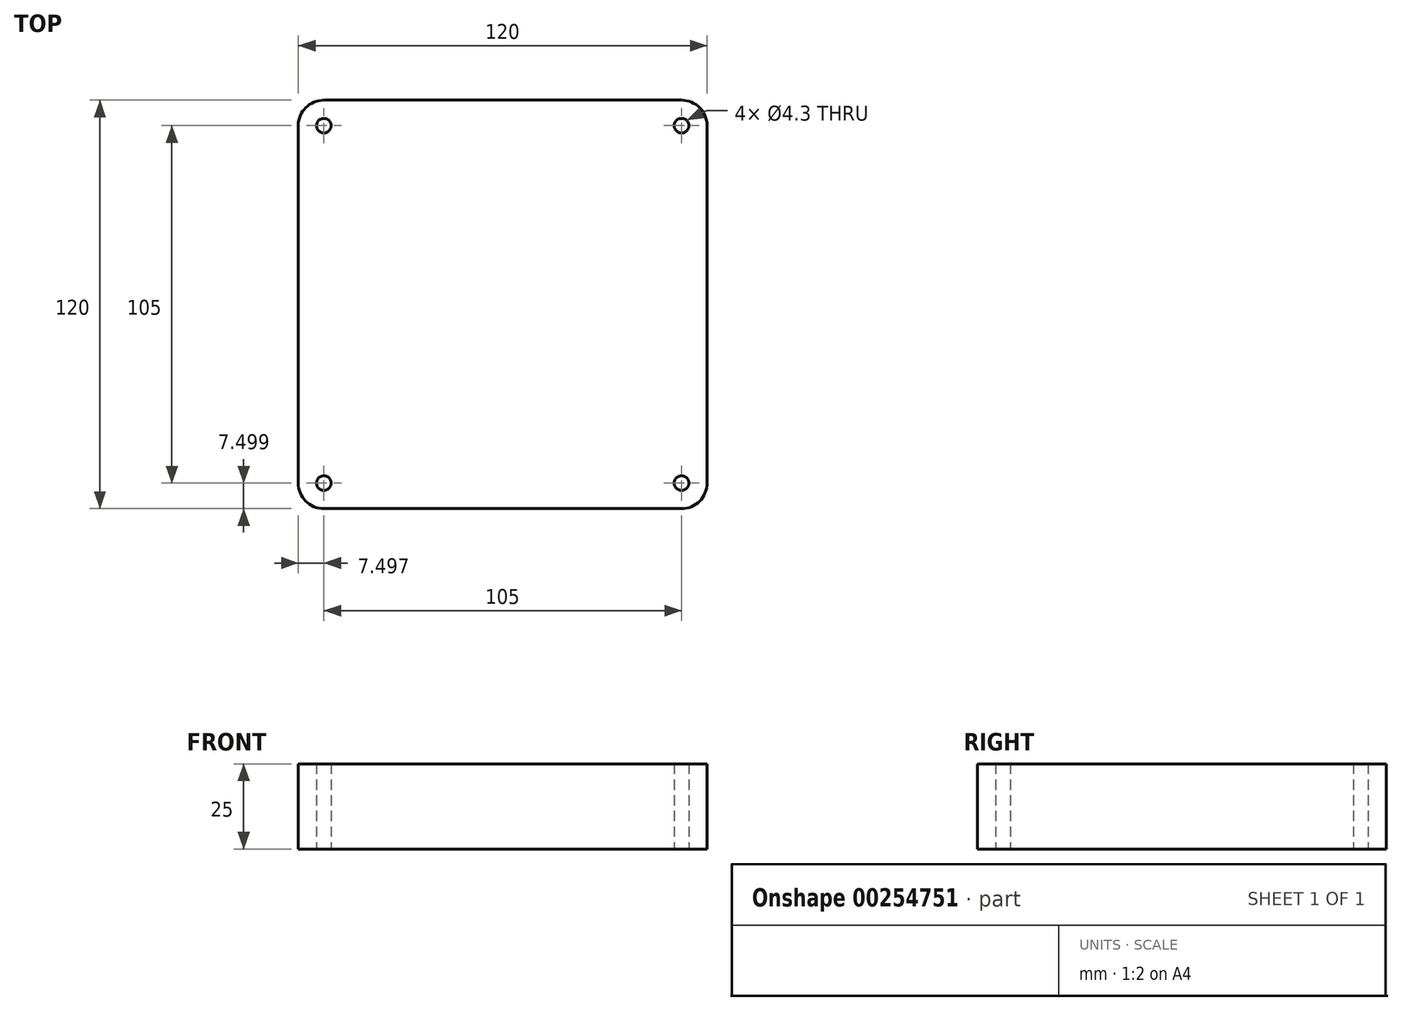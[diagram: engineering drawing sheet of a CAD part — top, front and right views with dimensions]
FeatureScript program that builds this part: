
annotation { "Feature Type Name" : "Feature", "Feature Type Description" : "" }
export const myFeature = defineFeature(function(context is Context, id is Id, definition is map)
    precondition{}
    {
        {
            var Q0;
            Q0=qCreatedBy(makeId("Top.planeOp"),FACE);
            var sketch = newSketch(context, id + "F0", { "sketchPlane" : qUnion([Q0])});
            skLineSegment(sketch, "E0.bottom", {"start": v(-52.14, 49.13) * mm, "end": v(52.86, 49.13) * mm});
            skLineSegment(sketch, "E0.top", {"start": v(-52.14, -70.87) * mm, "end": v(52.86, -70.87) * mm});
            skLineSegment(sketch, "E0.left", {"start": v(-59.64, 41.63) * mm, "end": v(-59.64, -63.37) * mm});
            skLineSegment(sketch, "E0.right", {"start": v(60.36, 41.63) * mm, "end": v(60.36, -63.37) * mm});
            skCircle(sketch, "E1", {"center": v(-52.14, 41.63) * mm, "radius": 2.15 * mm});
            skCircle(sketch, "E2", {"center": v(52.86, 41.63) * mm, "radius": 2.15 * mm});
            skCircle(sketch, "E3", {"center": v(-52.14, -63.37) * mm, "radius": 2.15 * mm});
            skCircle(sketch, "E4", {"center": v(52.86, -63.37) * mm, "radius": 2.15 * mm});
            skLineSegment(sketch, "E5", {"start": v(-52.14, 41.63) * mm, "end": v(-52.14, -82.45) * mm, "construction": true});
            skLineSegment(sketch, "E6", {"start": v(-52.14, -82.45) * mm, "end": v(-52.14, 41.63) * mm, "construction": true});
            skLineSegment(sketch, "E7", {"start": v(69.78, 41.63) * mm, "end": v(-52.14, 41.63) * mm, "construction": true});
            skLineSegment(sketch, "E8", {"start": v(70.66, -63.37) * mm, "end": v(-88.87, -63.37) * mm, "construction": true});
            skLineSegment(sketch, "E9", {"start": v(-88.87, -63.37) * mm, "end": v(52.86, -63.37) * mm, "construction": true});
            skLineSegment(sketch, "E10", {"start": v(52.86, -63.37) * mm, "end": v(52.86, 58.66) * mm, "construction": true});
            skPoint(sketch, "E11.visualSharp", {"position": v(-59.64, 49.13) * mm});
            skArc(sketch, "E11.filletArc", {"start": v(-52.14, 49.13) * mm, "mid": v(-57.45, 46.93) * mm, "end": v(-59.64, 41.63) * mm});
            skPoint(sketch, "E12.visualSharp", {"position": v(-59.64, -70.87) * mm});
            skArc(sketch, "E12.filletArc", {"start": v(-59.64, -63.37) * mm, "mid": v(-57.45, -68.67) * mm, "end": v(-52.14, -70.87) * mm});
            skPoint(sketch, "E13.visualSharp", {"position": v(60.36, -70.87) * mm});
            skArc(sketch, "E13.filletArc", {"start": v(52.86, -70.87) * mm, "mid": v(58.16, -68.67) * mm, "end": v(60.36, -63.37) * mm});
            skPoint(sketch, "E14.visualSharp", {"position": v(60.36, 49.13) * mm});
            skArc(sketch, "E14.filletArc", {"start": v(60.36, 41.63) * mm, "mid": v(58.16, 46.93) * mm, "end": v(52.86, 49.13) * mm});
            skSolve(sketch);
        }
        {
            var Q0;
            Q0=makeQuery(id+"F0.imprint","IMPRINT",FACE,{"disambiguationData":[TD([[makeQuery(id+"F0.imprint","IMPRINT",EDGE,{"derivedFrom":sQuery(id+"F0.wireOp",EDGE,"E0.bottom")}),-1.0]])]});
            extrude(context, id + "F1", {"entities" : qUnion([Q0]), "depth" : 25 * mm});
        }
    });
